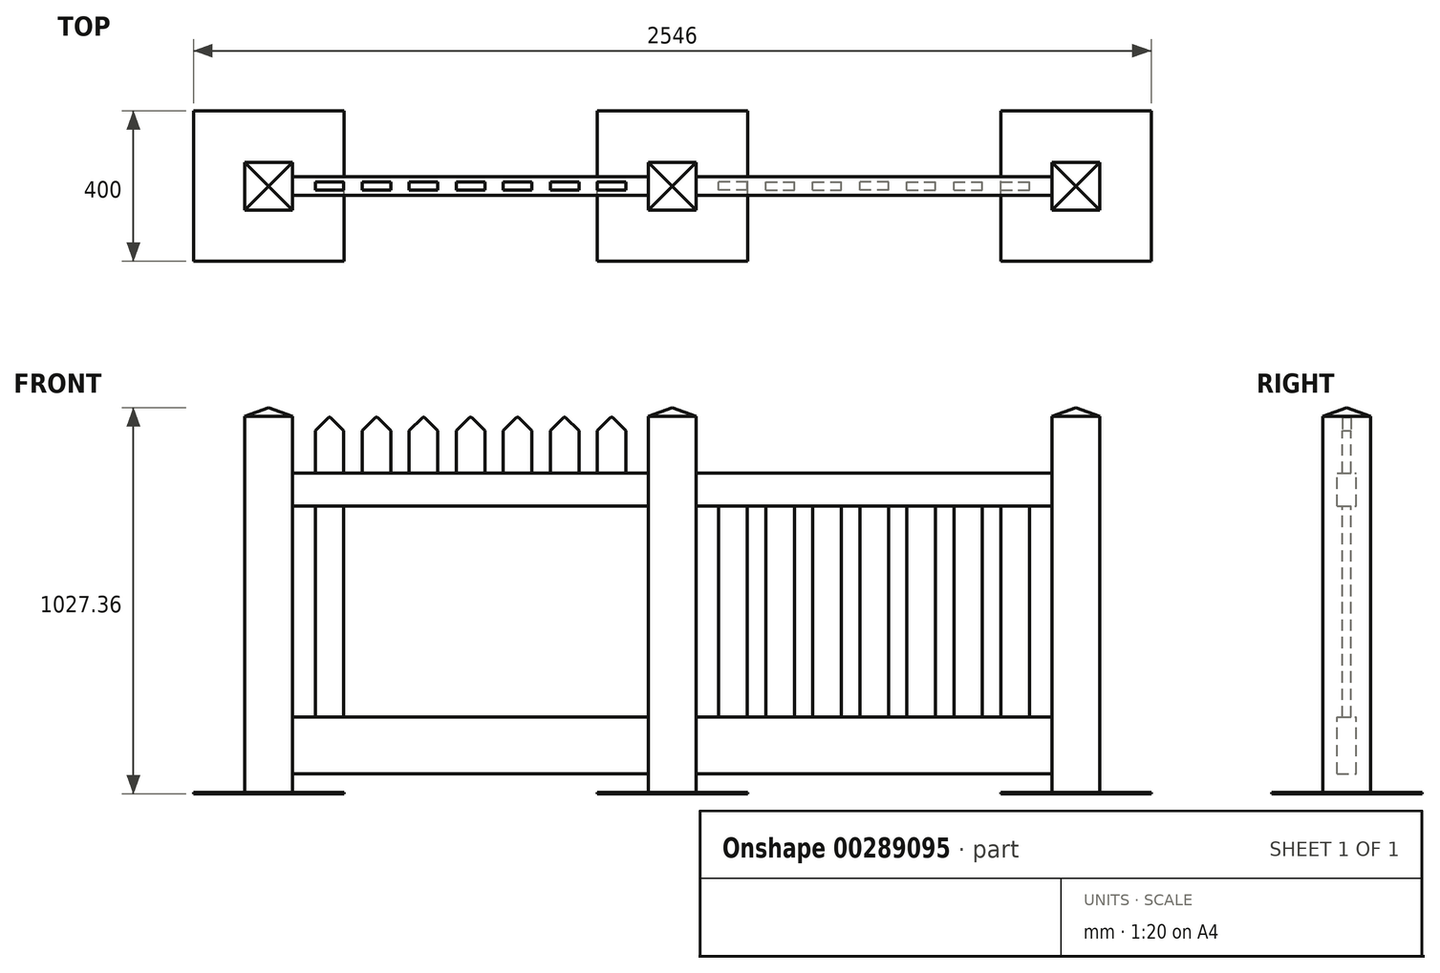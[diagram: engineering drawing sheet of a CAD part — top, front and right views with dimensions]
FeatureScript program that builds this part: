
annotation { "Feature Type Name" : "Feature", "Feature Type Description" : "" }
export const myFeature = defineFeature(function(context is Context, id is Id, definition is map)
    precondition{}
    {
        {
            var Q0;
            Q0=qCreatedBy(makeId("Front.planeOp"),FACE);
            var sketch = newSketch(context, id + "F0", { "sketchPlane" : qUnion([Q0])});
            skLineSegment(sketch, "E0.right", {"start": v(-597.77, -500) * mm, "end": v(-597.77, 500) * mm});
            skPoint(sketch, "E0.middle", {"position": v(0, 0) * mm});
            skLineSegment(sketch, "E1", {"start": v(-724.77, 500) * mm, "end": v(-724.77, -500) * mm});
            skLineSegment(sketch, "E2", {"start": v(-724.77, -500) * mm, "end": v(-597.77, -500) * mm});
            skLineSegment(sketch, "E3", {"start": v(-597.77, 350) * mm, "end": v(348.23, 350) * mm});
            skLineSegment(sketch, "E4", {"start": v(-597.77, 262) * mm, "end": v(348.23, 262) * mm});
            skLineSegment(sketch, "E5", {"start": v(-597.77, -450) * mm, "end": v(348.23, -450) * mm});
            skLineSegment(sketch, "E6", {"start": v(-597.77, -300) * mm, "end": v(348.23, -300) * mm});
            skLineSegment(sketch, "E7", {"start": v(-537.77, -300) * mm, "end": v(-537.77, 262) * mm});
            skLineSegment(sketch, "E8", {"start": v(-537.77, 462) * mm, "end": v(-503.3, 496.46) * mm});
            skLineSegment(sketch, "E9", {"start": v(-496.23, 496.46) * mm, "end": v(-461.77, 462) * mm});
            skLineSegment(sketch, "E10", {"start": v(-461.77, 462) * mm, "end": v(-461.77, 350) * mm});
            skLineSegment(sketch, "E11", {"start": v(-461.77, -300) * mm, "end": v(-537.77, -300) * mm});
            skLineSegment(sketch, "E12", {"start": v(348.23, 500) * mm, "end": v(348.23, -500) * mm});
            skLineSegment(sketch, "E13", {"start": v(475.23, 500) * mm, "end": v(475.23, -500) * mm});
            skLineSegment(sketch, "E14", {"start": v(475.23, -500) * mm, "end": v(348.23, -500) * mm});
            skLineSegment(sketch, "E15.1.0.0", {"start": v(-336.77, -300) * mm, "end": v(-412.77, -300) * mm});
            skLineSegment(sketch, "E15.1.0.1", {"start": v(-336.77, 462) * mm, "end": v(-336.77, 350) * mm});
            skLineSegment(sketch, "E15.1.0.2", {"start": v(-412.77, -300) * mm, "end": v(-412.77, 262) * mm});
            skLineSegment(sketch, "E15.1.0.3", {"start": v(-371.23, 496.46) * mm, "end": v(-336.77, 462) * mm});
            skLineSegment(sketch, "E15.1.0.4", {"start": v(-412.77, 462) * mm, "end": v(-378.3, 496.46) * mm});
            skLineSegment(sketch, "E15.2.0.0", {"start": v(-211.77, -300) * mm, "end": v(-287.77, -300) * mm});
            skLineSegment(sketch, "E15.2.0.1", {"start": v(-211.77, 462) * mm, "end": v(-211.77, 350) * mm});
            skLineSegment(sketch, "E15.2.0.2", {"start": v(-287.77, -300) * mm, "end": v(-287.77, 262) * mm});
            skLineSegment(sketch, "E15.2.0.3", {"start": v(-246.23, 496.46) * mm, "end": v(-211.77, 462) * mm});
            skLineSegment(sketch, "E15.2.0.4", {"start": v(-287.77, 462) * mm, "end": v(-253.3, 496.46) * mm});
            skLineSegment(sketch, "E15.3.0.0", {"start": v(-86.77, -300) * mm, "end": v(-162.77, -300) * mm});
            skLineSegment(sketch, "E15.3.0.1", {"start": v(-86.77, 462) * mm, "end": v(-86.77, 350) * mm});
            skLineSegment(sketch, "E15.3.0.2", {"start": v(-162.77, -300) * mm, "end": v(-162.77, 262) * mm});
            skLineSegment(sketch, "E15.3.0.3", {"start": v(-121.23, 496.46) * mm, "end": v(-86.77, 462) * mm});
            skLineSegment(sketch, "E15.3.0.4", {"start": v(-162.77, 462) * mm, "end": v(-128.3, 496.46) * mm});
            skLineSegment(sketch, "E15.4.0.0", {"start": v(38.23, -300) * mm, "end": v(-37.77, -300) * mm});
            skLineSegment(sketch, "E15.4.0.1", {"start": v(38.23, 462) * mm, "end": v(38.23, 350) * mm});
            skLineSegment(sketch, "E15.4.0.2", {"start": v(-37.77, -300) * mm, "end": v(-37.77, 262) * mm});
            skLineSegment(sketch, "E15.4.0.3", {"start": v(3.77, 496.46) * mm, "end": v(38.23, 462) * mm});
            skLineSegment(sketch, "E15.4.0.4", {"start": v(-37.77, 462) * mm, "end": v(-3.3, 496.46) * mm});
            skLineSegment(sketch, "E15.5.0.0", {"start": v(163.23, -300) * mm, "end": v(87.23, -300) * mm});
            skLineSegment(sketch, "E15.5.0.1", {"start": v(163.23, 462) * mm, "end": v(163.23, 350) * mm});
            skLineSegment(sketch, "E15.5.0.2", {"start": v(87.23, -300) * mm, "end": v(87.23, 262) * mm});
            skLineSegment(sketch, "E15.5.0.3", {"start": v(128.77, 496.46) * mm, "end": v(163.23, 462) * mm});
            skLineSegment(sketch, "E15.5.0.4", {"start": v(87.23, 462) * mm, "end": v(121.7, 496.46) * mm});
            skLineSegment(sketch, "E15.6.0.0", {"start": v(288.23, -300) * mm, "end": v(212.23, -300) * mm});
            skLineSegment(sketch, "E15.6.0.1", {"start": v(288.23, 462) * mm, "end": v(288.23, 350) * mm});
            skLineSegment(sketch, "E15.6.0.2", {"start": v(212.23, -300) * mm, "end": v(212.23, 262) * mm});
            skLineSegment(sketch, "E15.6.0.3", {"start": v(253.77, 496.46) * mm, "end": v(288.23, 462) * mm});
            skLineSegment(sketch, "E15.6.0.4", {"start": v(212.23, 462) * mm, "end": v(246.7, 496.46) * mm});
            skLineSegment(sketch, "E15.direction1", {"start": v(-537.77, -300) * mm, "end": v(-412.77, -300) * mm, "construction": true});
            skLineSegment(sketch, "E16.trimOffspring", {"start": v(-537.77, 350) * mm, "end": v(-537.77, 462) * mm});
            skLineSegment(sketch, "E17.trimOffspring", {"start": v(-461.77, 262) * mm, "end": v(-461.77, -300) * mm});
            skLineSegment(sketch, "E18.trimOffspring", {"start": v(288.23, 262) * mm, "end": v(288.23, -300) * mm});
            skLineSegment(sketch, "E19.trimOffspring", {"start": v(212.23, 350) * mm, "end": v(212.23, 462) * mm});
            skLineSegment(sketch, "E20.trimOffspring", {"start": v(163.23, 262) * mm, "end": v(163.23, -300) * mm});
            skLineSegment(sketch, "E21.trimOffspring", {"start": v(87.23, 350) * mm, "end": v(87.23, 462) * mm});
            skLineSegment(sketch, "E22.trimOffspring", {"start": v(38.23, 262) * mm, "end": v(38.23, -300) * mm});
            skLineSegment(sketch, "E23.trimOffspring", {"start": v(-37.77, 350) * mm, "end": v(-37.77, 462) * mm});
            skLineSegment(sketch, "E24.trimOffspring", {"start": v(-86.77, 262) * mm, "end": v(-86.77, -300) * mm});
            skLineSegment(sketch, "E25.trimOffspring", {"start": v(-162.77, 350) * mm, "end": v(-162.77, 462) * mm});
            skLineSegment(sketch, "E26.trimOffspring", {"start": v(-211.77, 262) * mm, "end": v(-211.77, -300) * mm});
            skLineSegment(sketch, "E27.trimOffspring", {"start": v(-287.77, 350) * mm, "end": v(-287.77, 462) * mm});
            skLineSegment(sketch, "E28.trimOffspring", {"start": v(-336.77, 262) * mm, "end": v(-336.77, -300) * mm});
            skLineSegment(sketch, "E29.trimOffspring", {"start": v(-412.77, 350) * mm, "end": v(-412.77, 462) * mm});
            skLineSegment(sketch, "E30", {"start": v(-724.77, 500) * mm, "end": v(-661.27, 523.4) * mm});
            skPoint(sketch, "E30.endSnap0", {"position": v(-661.27, 500) * mm});
            skLineSegment(sketch, "E31", {"start": v(-661.27, 523.4) * mm, "end": v(-597.77, 500) * mm});
            skLineSegment(sketch, "E32", {"start": v(348.23, 500) * mm, "end": v(411.73, 523.4) * mm});
            skPoint(sketch, "E32.endSnap0", {"position": v(411.73, 500) * mm});
            skLineSegment(sketch, "E33", {"start": v(411.73, 523.4) * mm, "end": v(475.23, 500) * mm});
            skPoint(sketch, "E34.orphan", {"position": v(-890.97, 523.4) * mm});
            skPoint(sketch, "E35.visualSharp", {"position": v(-499.77, 500) * mm});
            skPoint(sketch, "E36.visualSharp", {"position": v(-374.77, 500) * mm});
            skArc(sketch, "E36.filletArc", {"start": v(-371.23, 496.46) * mm, "mid": v(-374.77, 497.93) * mm, "end": v(-378.3, 496.46) * mm});
            skArc(sketch, "E37.filletArc", {"start": v(-496.23, 496.46) * mm, "mid": v(-499.77, 497.93) * mm, "end": v(-503.3, 496.46) * mm});
            skPoint(sketch, "E38.visualSharp", {"position": v(-249.77, 500) * mm});
            skArc(sketch, "E38.filletArc", {"start": v(-246.23, 496.46) * mm, "mid": v(-249.77, 497.93) * mm, "end": v(-253.3, 496.46) * mm});
            skPoint(sketch, "E39.visualSharp", {"position": v(-124.77, 500) * mm});
            skArc(sketch, "E39.filletArc", {"start": v(-121.23, 496.46) * mm, "mid": v(-124.77, 497.93) * mm, "end": v(-128.3, 496.46) * mm});
            skPoint(sketch, "E40.visualSharp", {"position": v(250.23, 500) * mm});
            skArc(sketch, "E40.filletArc", {"start": v(253.77, 496.46) * mm, "mid": v(250.23, 497.93) * mm, "end": v(246.7, 496.46) * mm});
            skPoint(sketch, "E41.visualSharp", {"position": v(125.23, 500) * mm});
            skArc(sketch, "E41.filletArc", {"start": v(128.77, 496.46) * mm, "mid": v(125.23, 497.93) * mm, "end": v(121.7, 496.46) * mm});
            skPoint(sketch, "E42.visualSharp", {"position": v(0.23, 500) * mm});
            skArc(sketch, "E42.filletArc", {"start": v(3.77, 496.46) * mm, "mid": v(0.23, 497.93) * mm, "end": v(-3.3, 496.46) * mm});
            skLineSegment(sketch, "E43", {"start": v(-861.27, -500) * mm, "end": v(-461.27, -500) * mm});
            skPoint(sketch, "E43.endSnap0", {"position": v(-661.27, -500) * mm});
            skLineSegment(sketch, "E44", {"start": v(-461.27, -500) * mm, "end": v(-461.27, -504) * mm});
            skLineSegment(sketch, "E45", {"start": v(-461.27, -504) * mm, "end": v(-861.27, -504) * mm});
            skLineSegment(sketch, "E46", {"start": v(-861.27, -504) * mm, "end": v(-861.27, -500) * mm});
            skLineSegment(sketch, "E47", {"start": v(411.73, -500) * mm, "end": v(211.73, -500) * mm});
            skLineSegment(sketch, "E48", {"start": v(211.73, -500) * mm, "end": v(211.73, -504) * mm});
            skLineSegment(sketch, "E49", {"start": v(211.73, -504) * mm, "end": v(611.73, -504) * mm});
            skLineSegment(sketch, "E50", {"start": v(611.73, -504) * mm, "end": v(611.73, -500) * mm});
            skLineSegment(sketch, "E51", {"start": v(611.73, -500) * mm, "end": v(475.23, -500) * mm});
            skLineSegment(sketch, "E52", {"start": v(411.73, 523.4) * mm, "end": v(411.73, 500) * mm});
            skArc(sketch, "E53.MirrorCS", {"start": v(569.7, 496.46) * mm, "mid": v(573.23, 497.93) * mm, "end": v(576.77, 496.46) * mm});
            skArc(sketch, "E54.MirrorCS", {"start": v(1194.7, 496.46) * mm, "mid": v(1198.23, 497.93) * mm, "end": v(1201.77, 496.46) * mm});
            skArc(sketch, "E55.MirrorCS", {"start": v(1319.7, 496.46) * mm, "mid": v(1323.23, 497.93) * mm, "end": v(1326.77, 496.46) * mm});
            skArc(sketch, "E56.MirrorCS", {"start": v(819.7, 496.46) * mm, "mid": v(823.23, 497.93) * mm, "end": v(826.77, 496.46) * mm});
            skArc(sketch, "E57.MirrorCS", {"start": v(1069.7, 496.46) * mm, "mid": v(1073.23, 497.93) * mm, "end": v(1076.77, 496.46) * mm});
            skArc(sketch, "E58.MirrorCS", {"start": v(944.7, 496.46) * mm, "mid": v(948.23, 497.93) * mm, "end": v(951.77, 496.46) * mm});
            skArc(sketch, "E59.MirrorCS", {"start": v(694.7, 496.46) * mm, "mid": v(698.23, 497.93) * mm, "end": v(701.77, 496.46) * mm});
            skLineSegment(sketch, "E60.MirrorCS", {"start": v(569.7, 496.46) * mm, "end": v(535.23, 462) * mm});
            skLineSegment(sketch, "E61.MirrorCS", {"start": v(986.23, 462) * mm, "end": v(951.77, 496.46) * mm});
            skLineSegment(sketch, "E62.MirrorCS", {"start": v(736.23, 462) * mm, "end": v(701.77, 496.46) * mm});
            skLineSegment(sketch, "E63.MirrorCS", {"start": v(1284.73, -500) * mm, "end": v(1284.73, -504) * mm});
            skLineSegment(sketch, "E64.MirrorCS", {"start": v(611.23, 462) * mm, "end": v(576.77, 496.46) * mm});
            skLineSegment(sketch, "E65.MirrorCS", {"start": v(819.7, 496.46) * mm, "end": v(785.23, 462) * mm});
            skLineSegment(sketch, "E66.MirrorCS", {"start": v(694.7, 496.46) * mm, "end": v(660.23, 462) * mm});
            skLineSegment(sketch, "E67.MirrorCS", {"start": v(1111.23, 462) * mm, "end": v(1076.77, 496.46) * mm});
            skLineSegment(sketch, "E68.MirrorCS", {"start": v(944.7, 496.46) * mm, "end": v(910.23, 462) * mm});
            skLineSegment(sketch, "E69.MirrorCS", {"start": v(1319.7, 496.46) * mm, "end": v(1285.23, 462) * mm});
            skLineSegment(sketch, "E70.MirrorCS", {"start": v(861.23, 462) * mm, "end": v(826.77, 496.46) * mm});
            skLineSegment(sketch, "E71.MirrorCS", {"start": v(611.73, -500) * mm, "end": v(611.73, -504) * mm});
            skLineSegment(sketch, "E72.MirrorCS", {"start": v(1684.73, -504) * mm, "end": v(1684.73, -500) * mm});
            skLineSegment(sketch, "E73.MirrorCS", {"start": v(1236.23, 462) * mm, "end": v(1201.77, 496.46) * mm});
            skLineSegment(sketch, "E74.MirrorCS", {"start": v(1194.7, 496.46) * mm, "end": v(1160.23, 462) * mm});
            skLineSegment(sketch, "E75.MirrorCS", {"start": v(1361.23, 462) * mm, "end": v(1326.77, 496.46) * mm});
            skLineSegment(sketch, "E76.MirrorCS", {"start": v(1069.7, 496.46) * mm, "end": v(1035.23, 462) * mm});
            skLineSegment(sketch, "E77.MirrorCS", {"start": v(1484.73, 523.4) * mm, "end": v(1421.23, 500) * mm});
            skLineSegment(sketch, "E78.MirrorCS", {"start": v(1548.23, 500) * mm, "end": v(1484.73, 523.4) * mm});
            skLineSegment(sketch, "E79.MirrorCS", {"start": v(1035.23, -300) * mm, "end": v(1111.23, -300) * mm});
            skLineSegment(sketch, "E80.MirrorCS", {"start": v(1160.23, -300) * mm, "end": v(1236.23, -300) * mm});
            skLineSegment(sketch, "E81.MirrorCS", {"start": v(1285.23, -300) * mm, "end": v(1361.23, -300) * mm});
            skLineSegment(sketch, "E82.MirrorCS", {"start": v(660.23, -300) * mm, "end": v(736.23, -300) * mm});
            skLineSegment(sketch, "E83.MirrorCS", {"start": v(785.23, -300) * mm, "end": v(861.23, -300) * mm});
            skLineSegment(sketch, "E84.MirrorCS", {"start": v(1548.23, -500) * mm, "end": v(1421.23, -500) * mm});
            skLineSegment(sketch, "E85.MirrorCS", {"start": v(1361.23, -300) * mm, "end": v(1236.23, -300) * mm, "construction": true});
            skLineSegment(sketch, "E86.MirrorCS", {"start": v(660.23, 462) * mm, "end": v(660.23, 350) * mm});
            skLineSegment(sketch, "E87.MirrorCS", {"start": v(785.23, 262) * mm, "end": v(785.23, -300) * mm});
            skLineSegment(sketch, "E88.MirrorCS", {"start": v(910.23, 462) * mm, "end": v(910.23, 350) * mm});
            skLineSegment(sketch, "E89.MirrorCS", {"start": v(861.23, -300) * mm, "end": v(861.23, 262) * mm});
            skLineSegment(sketch, "E90.MirrorCS", {"start": v(535.23, 262) * mm, "end": v(535.23, -300) * mm});
            skLineSegment(sketch, "E91.MirrorCS", {"start": v(1160.23, 462) * mm, "end": v(1160.23, 350) * mm});
            skPoint(sketch, "E92.MirrorP", {"position": v(698.23, 500) * mm});
            skLineSegment(sketch, "E93.MirrorCS", {"start": v(611.73, -504) * mm, "end": v(211.73, -504) * mm});
            skLineSegment(sketch, "E94.MirrorCS", {"start": v(861.23, 350) * mm, "end": v(861.23, 462) * mm});
            skLineSegment(sketch, "E95.MirrorCS", {"start": v(1236.23, 350) * mm, "end": v(1236.23, 462) * mm});
            skLineSegment(sketch, "E96.MirrorCS", {"start": v(348.23, -500) * mm, "end": v(475.23, -500) * mm});
            skLineSegment(sketch, "E97.MirrorCS", {"start": v(1361.23, 350) * mm, "end": v(1361.23, 462) * mm});
            skLineSegment(sketch, "E98.MirrorCS", {"start": v(1548.23, 500) * mm, "end": v(1548.23, -500) * mm});
            skLineSegment(sketch, "E99.MirrorCS", {"start": v(660.23, 262) * mm, "end": v(660.23, -300) * mm});
            skLineSegment(sketch, "E100.MirrorCS", {"start": v(910.23, 262) * mm, "end": v(910.23, -300) * mm});
            skLineSegment(sketch, "E101.MirrorCS", {"start": v(1111.23, -300) * mm, "end": v(1111.23, 262) * mm});
            skLineSegment(sketch, "E102.MirrorCS", {"start": v(1421.23, 350) * mm, "end": v(475.23, 350) * mm});
            skLineSegment(sketch, "E103.MirrorCS", {"start": v(1035.23, 262) * mm, "end": v(1035.23, -300) * mm});
            skLineSegment(sketch, "E104.MirrorCS", {"start": v(1284.73, -504) * mm, "end": v(1684.73, -504) * mm});
            skLineSegment(sketch, "E105.MirrorCS", {"start": v(1111.23, 350) * mm, "end": v(1111.23, 462) * mm});
            skPoint(sketch, "E106.MirrorP", {"position": v(573.23, 500) * mm});
            skLineSegment(sketch, "E107.MirrorCS", {"start": v(736.23, -300) * mm, "end": v(736.23, 262) * mm});
            skLineSegment(sketch, "E108.MirrorCS", {"start": v(611.23, 350) * mm, "end": v(611.23, 462) * mm});
            skPoint(sketch, "E109.MirrorP", {"position": v(1484.73, -500) * mm});
            skPoint(sketch, "E110.MirrorP", {"position": v(1198.23, 500) * mm});
            skLineSegment(sketch, "E111.MirrorCS", {"start": v(986.23, 350) * mm, "end": v(986.23, 462) * mm});
            skLineSegment(sketch, "E112.MirrorCS", {"start": v(1421.23, -450) * mm, "end": v(475.23, -450) * mm});
            skLineSegment(sketch, "E113.MirrorCS", {"start": v(910.23, -300) * mm, "end": v(986.23, -300) * mm});
            skLineSegment(sketch, "E114.MirrorCS", {"start": v(475.23, 500) * mm, "end": v(411.73, 523.4) * mm});
            skLineSegment(sketch, "E115.MirrorCS", {"start": v(736.23, 350) * mm, "end": v(736.23, 462) * mm});
            skPoint(sketch, "E116.MirrorP", {"position": v(823.23, 500) * mm});
            skLineSegment(sketch, "E117.MirrorCS", {"start": v(1035.23, 462) * mm, "end": v(1035.23, 350) * mm});
            skLineSegment(sketch, "E118.MirrorCS", {"start": v(611.23, -300) * mm, "end": v(611.23, 262) * mm});
            skPoint(sketch, "E119.MirrorP", {"position": v(1073.23, 500) * mm});
            skPoint(sketch, "E120.MirrorP", {"position": v(823.47, 0) * mm});
            skLineSegment(sketch, "E121.MirrorCS", {"start": v(1285.23, 262) * mm, "end": v(1285.23, -300) * mm});
            skLineSegment(sketch, "E122.MirrorCS", {"start": v(1421.23, -500) * mm, "end": v(1421.23, 500) * mm});
            skPoint(sketch, "E123.MirrorP", {"position": v(948.23, 500) * mm});
            skLineSegment(sketch, "E124.MirrorCS", {"start": v(986.23, -300) * mm, "end": v(986.23, 262) * mm});
            skLineSegment(sketch, "E125.MirrorCS", {"start": v(1160.23, 262) * mm, "end": v(1160.23, -300) * mm});
            skLineSegment(sketch, "E126.MirrorCS", {"start": v(785.23, 462) * mm, "end": v(785.23, 350) * mm});
            skLineSegment(sketch, "E127.MirrorCS", {"start": v(1361.23, -300) * mm, "end": v(1361.23, 262) * mm});
            skLineSegment(sketch, "E128.MirrorCS", {"start": v(1421.23, 262) * mm, "end": v(475.23, 262) * mm});
            skLineSegment(sketch, "E129.MirrorCS", {"start": v(1421.23, -300) * mm, "end": v(475.23, -300) * mm});
            skPoint(sketch, "E130.MirrorP", {"position": v(1484.73, 500) * mm});
            skPoint(sketch, "E131.MirrorP", {"position": v(1714.44, 523.4) * mm});
            skLineSegment(sketch, "E132.MirrorCS", {"start": v(1285.23, 462) * mm, "end": v(1285.23, 350) * mm});
            skLineSegment(sketch, "E133.MirrorCS", {"start": v(411.73, -500) * mm, "end": v(611.73, -500) * mm});
            skLineSegment(sketch, "E134.MirrorCS", {"start": v(535.23, 462) * mm, "end": v(535.23, 350) * mm});
            skLineSegment(sketch, "E135.MirrorCS", {"start": v(1684.73, -500) * mm, "end": v(1284.73, -500) * mm});
            skPoint(sketch, "E136.MirrorP", {"position": v(1323.23, 500) * mm});
            skLineSegment(sketch, "E137.MirrorCS", {"start": v(535.23, -300) * mm, "end": v(611.23, -300) * mm});
            skLineSegment(sketch, "E138.MirrorCS", {"start": v(1236.23, -300) * mm, "end": v(1236.23, 262) * mm});
            skLineSegment(sketch, "E139.trimOffspring", {"start": v(411.73, -500) * mm, "end": v(411.73, -504) * mm});
            skPoint(sketch, "E140.orphan", {"position": v(411.73, 640.98) * mm});
            skSolve(sketch);
        }
        {
            var Q0;
            Q0=makeQuery(id+"F0.imprint","IMPRINT",FACE,{"disambiguationData":[TD([[makeQuery(id+"F0.imprint","IMPRINT",EDGE,{"derivedFrom":sQuery(id+"F0.wireOp",EDGE,"E13")}),-1.0]])]});
            var Q1;
            {var subQ6=sQuery(id+"F0.wireOp",EDGE,"E1");Q1=makeQuery(id+"F0.imprint","IMPRINT",FACE,{"disambiguationData":[TD([[makeQuery(id+"F0.imprint","IMPRINT",EDGE,{"derivedFrom":subQ6}),1.0]])]});}
            var Q2;
            {var subQ8=sQuery(id+"F0.wireOp",EDGE,"E32");Q2=makeQuery(id+"F0.imprint","IMPRINT",FACE,{"disambiguationData":[TD([[makeQuery(id+"F0.imprint","IMPRINT",EDGE,{"derivedFrom":subQ8}),-1.0]])]});}
            var Q3;
            {var subQ7=sQuery(id+"F0.wireOp",EDGE,"E77.MirrorCS");Q3=makeQuery(id+"F0.imprint","IMPRINT",FACE,{"disambiguationData":[TD([[makeQuery(id+"F0.imprint","IMPRINT",EDGE,{"derivedFrom":subQ7}),1.0]])]});}
            extrude(context, id + "F1", {"entities" : qUnion([Q0, Q1, Q2, Q3]), "depth" : 63.5 * mm, "hasSecondDirection" : true, "secondDirectionOppositeDirection" : true, "secondDirectionDepth" : 63.5 * mm});
        }
        {
            var Q0;
            {var subQ9=sQuery(id+"F0.wireOp",EDGE,"E5");Q0=makeQuery(id+"F0.imprint","IMPRINT",FACE,{"disambiguationData":[TD([[makeQuery(id+"F0.imprint","IMPRINT",EDGE,{"derivedFrom":subQ9}),1.0]])]});}
            var Q1;
            {var subQ6=sQuery(id+"F0.wireOp",EDGE,"E0.right");var subQ9=sQuery(id+"F0.wireOp",EDGE,"E3");var subQ19=makeQuery(id+"F0.imprint","INTERSECT",VERTEX,{"derivedFrom":[subQ6,subQ9]});Q1=makeQuery(id+"F0.imprint","IMPRINT",FACE,{"disambiguationData":[TD([[makeQuery(id+"F0.imprint","IMPRINT",EDGE,{"disambiguationData":[TD([[subQ19,1.0]])],"derivedFrom":subQ6}),-1.0]])]});}
            var Q2;
            {var subQ9=sQuery(id+"F0.wireOp",EDGE,"E102.MirrorCS");var subQ23=makeQuery(id+"F0.imprint","INTERSECT",VERTEX,{"derivedFrom":[sQuery(id+"F0.wireOp",EDGE,"E97.MirrorCS"),subQ9]});Q2=makeQuery(id+"F0.imprint","IMPRINT",FACE,{"disambiguationData":[TD([[makeQuery(id+"F0.imprint","IMPRINT",EDGE,{"disambiguationData":[TD([[subQ23,1.0]])],"derivedFrom":subQ9}),1.0]])]});}
            var Q3;
            {var subQ8=sQuery(id+"F0.wireOp",EDGE,"E112.MirrorCS");Q3=makeQuery(id+"F0.imprint","IMPRINT",FACE,{"disambiguationData":[TD([[makeQuery(id+"F0.imprint","IMPRINT",EDGE,{"derivedFrom":subQ8}),-1.0]])]});}
            extrude(context, id + "F2", {"entities" : qUnion([Q0, Q1, Q2, Q3]), "depth" : 25 * mm, "hasSecondDirection" : true, "secondDirectionOppositeDirection" : true, "secondDirectionDepth" : 25 * mm});
        }
        {
            var Q0;
            Q0=makeQuery(id+"F0.imprint","IMPRINT",FACE,{"disambiguationData":[TD([[makeQuery(id+"F0.imprint","IMPRINT",EDGE,{"derivedFrom":sQuery(id+"F0.wireOp",EDGE,"E15.6.0.0")}),-1.0]])]});
            var Q1;
            {var subQ0=sQuery(id+"F0.wireOp",EDGE,"E15.6.0.1");Q1=makeQuery(id+"F0.imprint","IMPRINT",FACE,{"disambiguationData":[TD([[makeQuery(id+"F0.imprint","IMPRINT",EDGE,{"derivedFrom":subQ0}),-1.0]])]});}
            var Q2;
            {var subQ1=sQuery(id+"F0.wireOp",EDGE,"E15.5.0.1");Q2=makeQuery(id+"F0.imprint","IMPRINT",FACE,{"disambiguationData":[TD([[makeQuery(id+"F0.imprint","IMPRINT",EDGE,{"derivedFrom":subQ1}),-1.0]])]});}
            var Q3;
            {var subQ0=sQuery(id+"F0.wireOp",EDGE,"E15.4.0.1");Q3=makeQuery(id+"F0.imprint","IMPRINT",FACE,{"disambiguationData":[TD([[makeQuery(id+"F0.imprint","IMPRINT",EDGE,{"derivedFrom":subQ0}),-1.0]])]});}
            var Q4;
            {var subQ0=sQuery(id+"F0.wireOp",EDGE,"E15.3.0.1");Q4=makeQuery(id+"F0.imprint","IMPRINT",FACE,{"disambiguationData":[TD([[makeQuery(id+"F0.imprint","IMPRINT",EDGE,{"derivedFrom":subQ0}),-1.0]])]});}
            var Q5;
            {var subQ1=sQuery(id+"F0.wireOp",EDGE,"E15.2.0.1");Q5=makeQuery(id+"F0.imprint","IMPRINT",FACE,{"disambiguationData":[TD([[makeQuery(id+"F0.imprint","IMPRINT",EDGE,{"derivedFrom":subQ1}),-1.0]])]});}
            var Q6;
            Q6=makeQuery(id+"F0.imprint","IMPRINT",FACE,{"disambiguationData":[TD([[makeQuery(id+"F0.imprint","IMPRINT",EDGE,{"derivedFrom":sQuery(id+"F0.wireOp",EDGE,"E8")}),-1.0]])]});
            var Q7;
            {var subQ0=sQuery(id+"F0.wireOp",EDGE,"E7");Q7=makeQuery(id+"F0.imprint","IMPRINT",FACE,{"disambiguationData":[TD([[makeQuery(id+"F0.imprint","IMPRINT",EDGE,{"derivedFrom":subQ0}),-1.0]])]});}
            var Q8;
            Q8=makeQuery(id+"F0.imprint","IMPRINT",FACE,{"disambiguationData":[TD([[makeQuery(id+"F0.imprint","IMPRINT",EDGE,{"derivedFrom":sQuery(id+"F0.wireOp",EDGE,"E15.1.0.0")}),-1.0]])]});
            var Q9;
            Q9=makeQuery(id+"F0.imprint","IMPRINT",FACE,{"disambiguationData":[TD([[makeQuery(id+"F0.imprint","IMPRINT",EDGE,{"derivedFrom":sQuery(id+"F0.wireOp",EDGE,"E15.2.0.0")}),-1.0]])]});
            var Q10;
            Q10=makeQuery(id+"F0.imprint","IMPRINT",FACE,{"disambiguationData":[TD([[makeQuery(id+"F0.imprint","IMPRINT",EDGE,{"derivedFrom":sQuery(id+"F0.wireOp",EDGE,"E15.3.0.0")}),-1.0]])]});
            var Q11;
            Q11=makeQuery(id+"F0.imprint","IMPRINT",FACE,{"disambiguationData":[TD([[makeQuery(id+"F0.imprint","IMPRINT",EDGE,{"derivedFrom":sQuery(id+"F0.wireOp",EDGE,"E15.4.0.0")}),-1.0]])]});
            var Q12;
            Q12=makeQuery(id+"F0.imprint","IMPRINT",FACE,{"disambiguationData":[TD([[makeQuery(id+"F0.imprint","IMPRINT",EDGE,{"derivedFrom":sQuery(id+"F0.wireOp",EDGE,"E15.5.0.0")}),-1.0]])]});
            var Q13;
            {var subQ0=sQuery(id+"F0.wireOp",EDGE,"E15.1.0.1");Q13=makeQuery(id+"F0.imprint","IMPRINT",FACE,{"disambiguationData":[TD([[makeQuery(id+"F0.imprint","IMPRINT",EDGE,{"derivedFrom":subQ0}),-1.0]])]});}
            var Q14;
            {var subQ0=sQuery(id+"F0.wireOp",EDGE,"E90.MirrorCS");Q14=makeQuery(id+"F0.imprint","IMPRINT",FACE,{"disambiguationData":[TD([[makeQuery(id+"F0.imprint","IMPRINT",EDGE,{"derivedFrom":subQ0}),1.0]])]});}
            var Q15;
            Q15=makeQuery(id+"F0.imprint","IMPRINT",FACE,{"disambiguationData":[TD([[makeQuery(id+"F0.imprint","IMPRINT",EDGE,{"derivedFrom":sQuery(id+"F0.wireOp",EDGE,"E53.MirrorCS")}),-1.0]])]});
            var Q16;
            Q16=makeQuery(id+"F0.imprint","IMPRINT",FACE,{"disambiguationData":[TD([[makeQuery(id+"F0.imprint","IMPRINT",EDGE,{"derivedFrom":sQuery(id+"F0.wireOp",EDGE,"E59.MirrorCS")}),-1.0]])]});
            var Q17;
            Q17=makeQuery(id+"F0.imprint","IMPRINT",FACE,{"disambiguationData":[TD([[makeQuery(id+"F0.imprint","IMPRINT",EDGE,{"derivedFrom":sQuery(id+"F0.wireOp",EDGE,"E56.MirrorCS")}),-1.0]])]});
            var Q18;
            Q18=makeQuery(id+"F0.imprint","IMPRINT",FACE,{"disambiguationData":[TD([[makeQuery(id+"F0.imprint","IMPRINT",EDGE,{"derivedFrom":sQuery(id+"F0.wireOp",EDGE,"E58.MirrorCS")}),-1.0]])]});
            var Q19;
            Q19=makeQuery(id+"F0.imprint","IMPRINT",FACE,{"disambiguationData":[TD([[makeQuery(id+"F0.imprint","IMPRINT",EDGE,{"derivedFrom":sQuery(id+"F0.wireOp",EDGE,"E57.MirrorCS")}),-1.0]])]});
            var Q20;
            Q20=makeQuery(id+"F0.imprint","IMPRINT",FACE,{"disambiguationData":[TD([[makeQuery(id+"F0.imprint","IMPRINT",EDGE,{"derivedFrom":sQuery(id+"F0.wireOp",EDGE,"E54.MirrorCS")}),-1.0]])]});
            var Q21;
            Q21=makeQuery(id+"F0.imprint","IMPRINT",FACE,{"disambiguationData":[TD([[makeQuery(id+"F0.imprint","IMPRINT",EDGE,{"derivedFrom":sQuery(id+"F0.wireOp",EDGE,"E55.MirrorCS")}),-1.0]])]});
            var Q22;
            {var subQ0=sQuery(id+"F0.wireOp",EDGE,"E121.MirrorCS");Q22=makeQuery(id+"F0.imprint","IMPRINT",FACE,{"disambiguationData":[TD([[makeQuery(id+"F0.imprint","IMPRINT",EDGE,{"derivedFrom":subQ0}),1.0]])]});}
            var Q23;
            {var subQ0=sQuery(id+"F0.wireOp",EDGE,"E125.MirrorCS");Q23=makeQuery(id+"F0.imprint","IMPRINT",FACE,{"disambiguationData":[TD([[makeQuery(id+"F0.imprint","IMPRINT",EDGE,{"derivedFrom":subQ0}),1.0]])]});}
            var Q24;
            {var subQ0=sQuery(id+"F0.wireOp",EDGE,"E101.MirrorCS");Q24=makeQuery(id+"F0.imprint","IMPRINT",FACE,{"disambiguationData":[TD([[makeQuery(id+"F0.imprint","IMPRINT",EDGE,{"derivedFrom":subQ0}),1.0]])]});}
            var Q25;
            {var subQ0=sQuery(id+"F0.wireOp",EDGE,"E100.MirrorCS");Q25=makeQuery(id+"F0.imprint","IMPRINT",FACE,{"disambiguationData":[TD([[makeQuery(id+"F0.imprint","IMPRINT",EDGE,{"derivedFrom":subQ0}),1.0]])]});}
            var Q26;
            {var subQ0=sQuery(id+"F0.wireOp",EDGE,"E87.MirrorCS");Q26=makeQuery(id+"F0.imprint","IMPRINT",FACE,{"disambiguationData":[TD([[makeQuery(id+"F0.imprint","IMPRINT",EDGE,{"derivedFrom":subQ0}),1.0]])]});}
            var Q27;
            {var subQ0=sQuery(id+"F0.wireOp",EDGE,"E99.MirrorCS");Q27=makeQuery(id+"F0.imprint","IMPRINT",FACE,{"disambiguationData":[TD([[makeQuery(id+"F0.imprint","IMPRINT",EDGE,{"derivedFrom":subQ0}),1.0]])]});}
            extrude(context, id + "F3", {"entities" : qUnion([Q0, Q1, Q2, Q3, Q4, Q5, Q6, Q7, Q8, Q9, Q10, Q11, Q12, Q13, Q14, Q15, Q16, Q17, Q18, Q19, Q20, Q21, Q22, Q23, Q24, Q25, Q26, Q27]), "depth" : 11 * mm, "hasSecondDirection" : true, "secondDirectionOppositeDirection" : true, "secondDirectionDepth" : 11 * mm});
        }
        {
            var Q0;
            {var subQ0=sQuery(id+"F0.wireOp",EDGE,"E44");Q0=makeQuery(id+"F0.imprint","IMPRINT",FACE,{"disambiguationData":[TD([[makeQuery(id+"F0.imprint","IMPRINT",EDGE,{"derivedFrom":subQ0}),-1.0]])]});}
            var Q1;
            {var subQ3=sQuery(id+"F0.wireOp",EDGE,"E14");Q1=makeQuery(id+"F0.imprint","IMPRINT",FACE,{"disambiguationData":[TD([[makeQuery(id+"F0.imprint","IMPRINT",EDGE,{"derivedFrom":subQ3}),1.0]])]});}
            var Q2;
            {var subQ1=sQuery(id+"F0.wireOp",EDGE,"E71.MirrorCS");Q2=makeQuery(id+"F0.imprint","IMPRINT",FACE,{"disambiguationData":[TD([[makeQuery(id+"F0.imprint","IMPRINT",EDGE,{"derivedFrom":subQ1}),-1.0]])]});}
            var Q3;
            Q3=makeQuery(id+"F0.imprint","IMPRINT",FACE,{"disambiguationData":[TD([[makeQuery(id+"F0.imprint","IMPRINT",EDGE,{"derivedFrom":sQuery(id+"F0.wireOp",EDGE,"E47")}),1.0]])]});
            var Q4;
            {var subQ3=sQuery(id+"F0.wireOp",EDGE,"E63.MirrorCS");Q4=makeQuery(id+"F0.imprint","IMPRINT",FACE,{"disambiguationData":[TD([[makeQuery(id+"F0.imprint","IMPRINT",EDGE,{"derivedFrom":subQ3}),1.0]])]});}
            extrude(context, id + "F4", {"entities" : qUnion([Q0, Q1, Q2, Q3, Q4]), "depth" : 200 * mm, "hasSecondDirection" : true, "secondDirectionOppositeDirection" : true, "secondDirectionDepth" : 200 * mm});
        }
        {
            var Q0;
            Q0=makeQuery(id+"F1.opExtrude","SWEPT_FACE",FACE,{"disambiguationData":[OSD([sQuery(id+"F0.wireOp",EDGE,"E98.MirrorCS")])]});
            var sketch = newSketch(context, id + "F5", { "sketchPlane" : qUnion([Q0])});
            skLineSegment(sketch, "E141", {"start": v(-63.5, 500) * mm, "end": v(0, 523.36) * mm});
            skLineSegment(sketch, "E142", {"start": v(0, 523.36) * mm, "end": v(63.5, 500) * mm});
            skLineSegment(sketch, "E143", {"start": v(63.5, 500) * mm, "end": v(67.97, 528.99) * mm});
            skLineSegment(sketch, "E144", {"start": v(67.97, 528.99) * mm, "end": v(-79.32, 530.86) * mm});
            skLineSegment(sketch, "E145", {"start": v(-79.32, 530.86) * mm, "end": v(-63.5, 500) * mm});
            skSolve(sketch);
        }
        {
            var Q0;
            Q0=makeQuery(id+"F5.imprint","IMPRINT",FACE,{"disambiguationData":[TD([[makeQuery(id+"F5.imprint","IMPRINT",EDGE,{"derivedFrom":sQuery(id+"F5.wireOp",EDGE,"E141")}),1.0]])]});
            extrude(context, id + "F6", {"entities" : qUnion([Q0]), "operationType" : NewBodyOperationType.REMOVE, "oppositeDirection" : true, "depth" : 5000 * mm});
        }
    });
